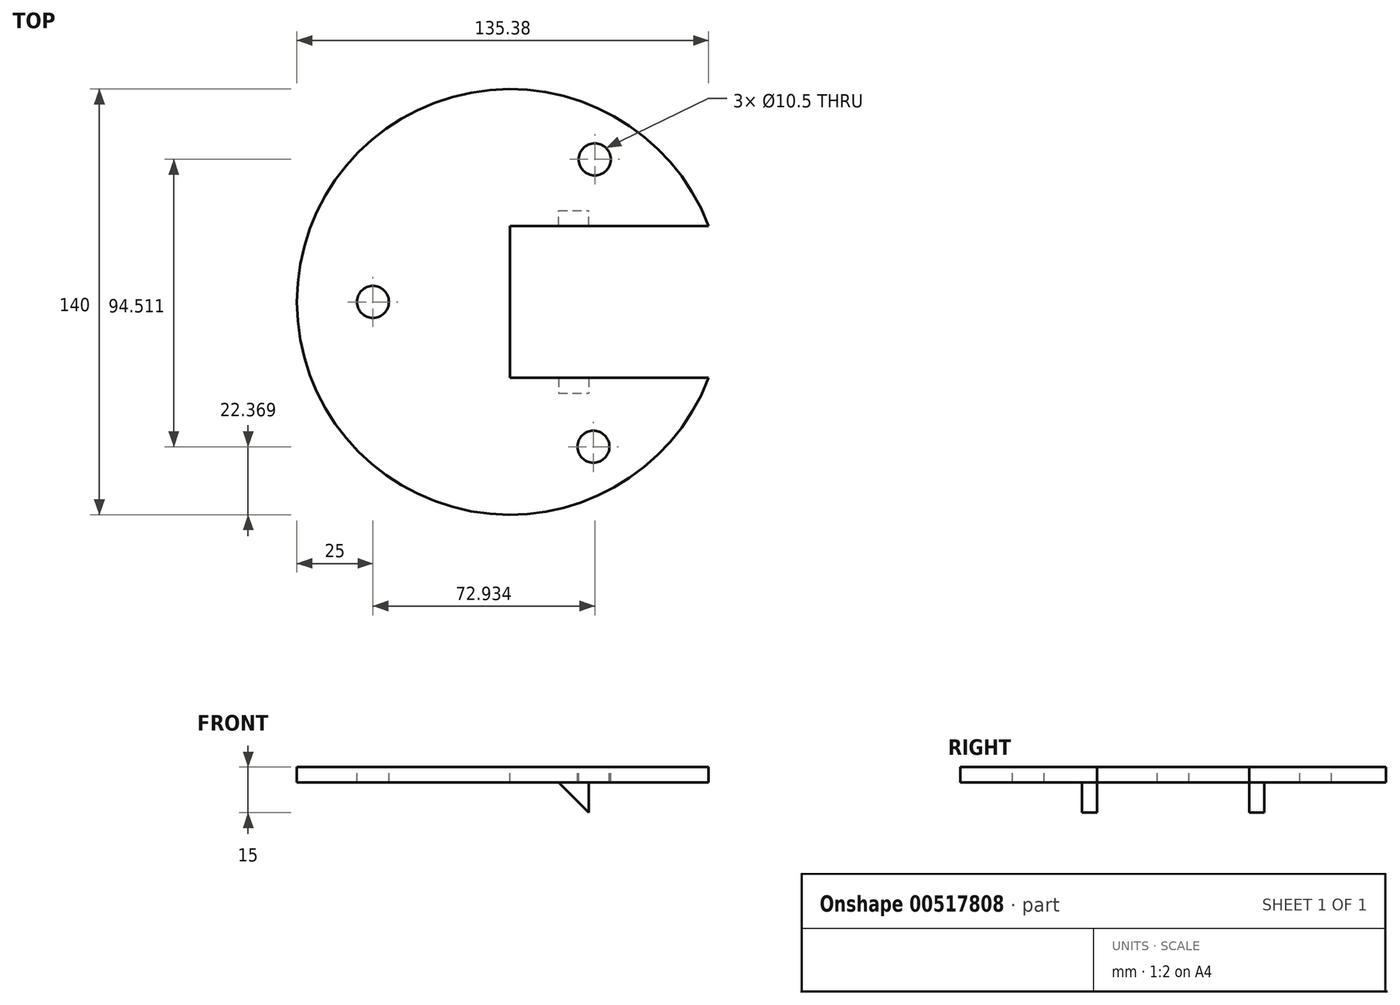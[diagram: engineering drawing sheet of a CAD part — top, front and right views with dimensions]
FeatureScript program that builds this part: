
annotation { "Feature Type Name" : "Feature", "Feature Type Description" : "" }
export const myFeature = defineFeature(function(context is Context, id is Id, definition is map)
    precondition{}
    {
        {
            var Q0;
            Q0=qCreatedBy(makeId("Top.planeOp"),FACE);
            var sketch = newSketch(context, id + "F0", { "sketchPlane" : qUnion([Q0])});
            skCircle(sketch, "E0", {"center": v(0, 0) * mm, "radius": 70 * mm});
            skSolve(sketch);
        }
        {
            var Q0;
            Q0 = qSketchRegion(id + "F0", true);
            extrude(context, id + "F1", {"entities" : qUnion([Q0]), "depth" : 5 * mm, "offsetDistance" : 25 * mm});
        }
        {
            var Q0;
            Q0=makeQuery(id+"F1.opExtrude","CAP_FACE",FACE,{"disambiguationData":[OSD([sQuery(id+"F0.wireOp",EDGE,"E0")])],"isStart":false});
            var sketch = newSketch(context, id + "F2", { "sketchPlane" : qUnion([Q0])});
            skLineSegment(sketch, "E1", {"start": v(0, 0) * mm, "end": v(-45, 0) * mm});
            skCircle(sketch, "E2", {"center": v(-45, 0) * mm, "radius": 5.25 * mm});
            skLineSegment(sketch, "E3", {"start": v(0, 0) * mm, "end": v(27.5, -47.63) * mm});
            skLineSegment(sketch, "E4", {"start": v(0.43, -0.75) * mm, "end": v(27.93, 46.88) * mm});
            skCircle(sketch, "E5", {"center": v(27.93, 46.88) * mm, "radius": 5.25 * mm});
            skCircle(sketch, "E6", {"center": v(27.5, -47.63) * mm, "radius": 5.25 * mm});
            skSolve(sketch);
        }
        {
            var Q0;
            Q0 = qSketchRegion(id + "F2", true);
            extrude(context, id + "F3", {"entities" : qUnion([Q0]), "operationType" : NewBodyOperationType.REMOVE, "oppositeDirection" : true, "depth" : 25 * mm, "offsetDistance" : 25 * mm});
        }
        {
            var Q0;
            Q0=makeQuery(id+"F1.opExtrude","CAP_FACE",FACE,{"disambiguationData":[OSD([sQuery(id+"F0.wireOp",EDGE,"E0")])],"isStart":false});
            var sketch = newSketch(context, id + "F4", { "sketchPlane" : qUnion([Q0])});
            skLineSegment(sketch, "E7.bottom", {"start": v(0, 25) * mm, "end": v(140, 25) * mm});
            skLineSegment(sketch, "E7.top", {"start": v(0, -25) * mm, "end": v(140, -25) * mm});
            skLineSegment(sketch, "E7.left", {"start": v(0, 25) * mm, "end": v(0, -25) * mm});
            skLineSegment(sketch, "E7.right", {"start": v(140, 25) * mm, "end": v(140, -25) * mm});
            skPoint(sketch, "E7.middle", {"position": v(70, 0) * mm});
            skSolve(sketch);
        }
        {
            var Q0;
            {var subQ0=sQuery(id+"F4.wireOp",EDGE,"E7.left");Q0=makeQuery(id+"F4.imprint","IMPRINT",FACE,{"disambiguationData":[TD([[makeQuery(id+"F4.imprint","IMPRINT",EDGE,{"derivedFrom":subQ0}),1.0]])]});}
            extrude(context, id + "F5", {"entities" : qUnion([Q0]), "operationType" : NewBodyOperationType.REMOVE, "oppositeDirection" : true, "depth" : 25 * mm, "offsetDistance" : 25 * mm});
        }
        {
            var Q0;
            Q0=makeQuery(id+"F1.opExtrude","CAP_FACE",FACE,{"disambiguationData":[OSD([sQuery(id+"F0.wireOp",EDGE,"E0")])],"isStart":true});
            var sketch = newSketch(context, id + "F6", { "sketchPlane" : qUnion([Q0])});
            skLineSegment(sketch, "E8", {"start": v(0, 25) * mm, "end": v(16, 25) * mm});
            skLineSegment(sketch, "E9", {"start": v(0, -25) * mm, "end": v(16, -25) * mm});
            skLineSegment(sketch, "E10.bottom", {"start": v(16, 25) * mm, "end": v(26, 25) * mm});
            skLineSegment(sketch, "E10.top", {"start": v(16, 30) * mm, "end": v(26, 30) * mm});
            skLineSegment(sketch, "E10.left", {"start": v(16, 25) * mm, "end": v(16, 30) * mm});
            skLineSegment(sketch, "E10.right", {"start": v(26, 25) * mm, "end": v(26, 30) * mm});
            skLineSegment(sketch, "E11.bottom", {"start": v(16, -25) * mm, "end": v(26, -25) * mm});
            skLineSegment(sketch, "E11.top", {"start": v(16, -30) * mm, "end": v(26, -30) * mm});
            skLineSegment(sketch, "E11.left", {"start": v(16, -25) * mm, "end": v(16, -30) * mm});
            skLineSegment(sketch, "E11.right", {"start": v(26, -25) * mm, "end": v(26, -30) * mm});
            skSolve(sketch);
        }
        {
            var Q0;
            Q0=makeQuery(id+"F6.imprint","IMPRINT",FACE,{"disambiguationData":[TD([[makeQuery(id+"F6.imprint","IMPRINT",EDGE,{"derivedFrom":sQuery(id+"F6.wireOp",EDGE,"E11.bottom")}),-1.0]])]});
            var Q1;
            Q1=makeQuery(id+"F6.imprint","IMPRINT",FACE,{"disambiguationData":[TD([[makeQuery(id+"F6.imprint","IMPRINT",EDGE,{"derivedFrom":sQuery(id+"F6.wireOp",EDGE,"E10.bottom")}),1.0]])]});
            extrude(context, id + "F7", {"entities" : qUnion([Q0, Q1]), "operationType" : NewBodyOperationType.ADD, "depth" : 10 * mm, "offsetDistance" : 25 * mm});
        }
        {
            var Q0;
            Q0=makeQuery(id+"F7.opExtrude","SWEPT_FACE",FACE,{"disambiguationData":[OSD([sQuery(id+"F6.wireOp",EDGE,"E11.top")])]});
            var sketch = newSketch(context, id + "F8", { "sketchPlane" : qUnion([Q0])});
            skLineSegment(sketch, "E12", {"start": v(-26, 0) * mm, "end": v(-16, -10) * mm});
            skLineSegment(sketch, "E13", {"start": v(-16, -10) * mm, "end": v(-26, -10) * mm});
            skLineSegment(sketch, "E14", {"start": v(-26, -10) * mm, "end": v(-16, 0) * mm});
            skCircle(sketch, "E15", {"center": v(-21, -5) * mm, "radius": 2.5 * mm});
            skSolve(sketch);
        }
        {
            var Q0;
            {var subQ0=sQuery(id+"F8.wireOp",EDGE,"E15");var subQ1=sQuery(id+"F8.wireOp",EDGE,"E12");var subQ2=makeQuery(id+"F8.imprint","INTERSECT",VERTEX,{"disambiguationData":[OD(0.0)],"derivedFrom":[subQ1,subQ0]});Q0=makeQuery(id+"F8.imprint","IMPRINT",FACE,{"disambiguationData":[TD([[makeQuery(id+"F8.imprint","IMPRINT",EDGE,{"disambiguationData":[TD([[subQ2,-1.0]])],"derivedFrom":subQ1}),-1.0]])]});}
            var Q1;
            {var subQ0=sQuery(id+"F8.wireOp",EDGE,"E14");var subQ1=sQuery(id+"F8.wireOp",EDGE,"E12");var subQ2=makeQuery(id+"F8.imprint","INTERSECT",VERTEX,{"derivedFrom":[subQ1,subQ0]});Q1=makeQuery(id+"F8.imprint","IMPRINT",FACE,{"disambiguationData":[TD([[makeQuery(id+"F8.imprint","IMPRINT",EDGE,{"disambiguationData":[TD([[subQ2,-1.0]])],"derivedFrom":subQ1}),1.0]])]});}
            var Q2;
            {var subQ0=sQuery(id+"F8.wireOp",EDGE,"E14");var subQ1=sQuery(id+"F8.wireOp",EDGE,"E12");var subQ2=makeQuery(id+"F8.imprint","INTERSECT",VERTEX,{"derivedFrom":[subQ1,subQ0]});Q2=makeQuery(id+"F8.imprint","IMPRINT",FACE,{"disambiguationData":[TD([[makeQuery(id+"F8.imprint","IMPRINT",EDGE,{"disambiguationData":[TD([[subQ2,-1.0]])],"derivedFrom":subQ1}),-1.0]])]});}
            var Q3;
            {var subQ0=sQuery(id+"F8.wireOp",EDGE,"E15");var subQ1=sQuery(id+"F8.wireOp",EDGE,"E12");var subQ2=makeQuery(id+"F8.imprint","INTERSECT",VERTEX,{"disambiguationData":[OD(0.0)],"derivedFrom":[subQ1,subQ0]});Q3=makeQuery(id+"F8.imprint","IMPRINT",FACE,{"disambiguationData":[TD([[makeQuery(id+"F8.imprint","IMPRINT",EDGE,{"disambiguationData":[TD([[subQ2,-1.0]])],"derivedFrom":subQ1}),1.0]])]});}
            extrude(context, id + "F9", {"entities" : qUnion([Q0, Q1, Q2, Q3]), "operationType" : NewBodyOperationType.REMOVE, "oppositeDirection" : true, "depth" : 75.4 * mm, "offsetDistance" : 25 * mm});
        }
    });
